# Revit family: Rolling_Shutter_Rulosec_EN
name_source: partatom
category: Doors
units: mm (PartAtom-declared; Revit-internal decimal feet)

## family parameters
Always vertical = Yes
Cut with Voids When Loaded = No
Host = Wall
OmniClass Number = 23.30.10.00
OmniClass Title = Doors
Room Calculation Point = No
Shared = No

## types (1)
- Rolling_Shutter_Rulosec_EN
    Acoustic insulation = without
    Analytic Construction = <Keine Auswahl>
    Application range (temperature) = -20°- 40°C
    Burglar protection = without
    Burglar protection Id = 1
    CAL_Abdeckung = No
    CAL_Ballendurchmesser = 102 mm
    CAL_H3 = 395 mm  [stored 1.29593 ft]
    CAL_H4 = 260 mm  [stored 0.853018 ft]
    CAL_Konsolen = Yes
    CAL_Maximal Breite = 7000 mm  [stored 22.9659 ft]
    CAL_Maximal Höhe = 5000 mm  [stored 16.4042 ft]
    CAL_Minimal Breite = 1000 mm  [stored 3.28084 ft]
    CAL_Minimal Höhe = 1000 mm  [stored 3.28084 ft]
    CAL_Profilabstand = 50 mm  [stored 0.164042 ft]
    CAL_Rohbaubreite = 3000 mm  [stored 9.84252 ft]
    CAL_Rohbauhöhe = 3000 mm  [stored 9.84252 ft]
    CAL_Torbehang Anzahl Torglieder = 63
    CAL_Torbehang Breite = 3053 mm  [stored 10.0164 ft]
    CAL_Torbehang Profil 50 = Yes
    CAL_Torbehang Profil 65 = No
    CAL_Void Höhe = 0 mm  [stored 0 ft]
    CAL_Wandabstand = 0 mm  [stored 0 ft]
    CE mark available = Yes
    Control type = key switch
    Control type Id = 3
    Cover type = without
    Cover type Id = 1
    Curtain = Aluminium
    Define Thermal Properties by = Schematic Type
    Door curtain material = Mesvac - RAL 9006
    Door curtain profile height = 50 mm  [stored 0.164042 ft]
    Door curtain type = 2500
    Door curtain type Id = 1
    Fire Rating = without
    Fitting depth = 260 mm  [stored 0.853018 ft]
    Fitting location, type = Interior walls
    Fitting location, type Id = 1
    Fitting type = behind the opening
    Fitting type Id = 1
    Floor structure height = 0 mm  [stored 0 ft]
    Frame = Aluminium
    Frame material = Mesvac - RAL 9006
    Function = Interior
    Headroom = 395 mm  [stored 1.29593 ft]
    Height = 3000 mm  [stored 9.84252 ft]
    Manufacturer = Mesvac Oy
    Model = Rulosec
    Operator position, type = right
    Operator position, type Id = 1
    Operator type = with
    Rough Height = 3000 mm  [stored 9.84252 ft]
    Rough Width = 3000 mm  [stored 9.84252 ft]
    URL = https://www.mesvac.fi
    URL 2 = https://www.mesvac.fi
    URL 3 = https://www.mesvac.fi
    Wall Closure = By host
    Wall distance = 0 mm  [stored 0 ft]
    Width = 3000 mm  [stored 9.84252 ft]
    Wind load class = Klasse 2

note: [stored X ft] marks values corroborated as IEEE doubles in the binary element streams (Revit-internal decimal feet)

## geometry (parser evidence)
native form markers: Sweep x13
no freeform markers — native parametric forms only
